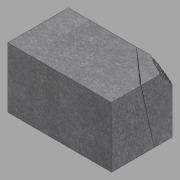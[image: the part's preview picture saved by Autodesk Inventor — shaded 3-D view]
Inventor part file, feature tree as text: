
AUTODESK INVENTOR PART (.ipt)
format: ipt  version: 2022.1 (Build 261234020, 234B)  size: 473,088 bytes
history: native  units: in
note: dims shown in document units (in); Inventor stores cm internally (conversion verified against a paired STEP export)
features: sketch x4, other x3, extrude x1, loft x1
ambient origin geometry x8: Origin, YZ Plane, XZ Plane, XY Plane, X Axis, Y Axis, Z Axis, Center Point
bodies: Solid1 (feature_tree)
feature tree (9):
  other  "2nd.ipt"
  sketch  "Sketch1"  dims[d0=0.3937in d1=1.0in d2=0.0in]
  extrude  "Extrusion1"  Depth=0.3937in TaperAngle=0.0deg
  loft  "Loft1"
  other  "Solid1::2nd.ipt"
  other  "TaggingFeature1"
  sketch  "Sketch2"  dims[d3=0.0in d4=90.0deg d5=0.0in d6=90.0deg]
  sketch  "Sketch3"
  sketch  "Sketch4"
